# Revit family: Fallrohrstütze DN 80 u. DN100-Set
name_source: partatom
category: HLS-Bauteile
revit_build: Autodesk Revit 2017 (Build: 20190507_1515(x64)
units: mm (PartAtom-declared; Revit-internal decimal feet)

## family parameters
Basisbauteil = Fläche
Beim Laden mit Abzugskörper schneiden = Nein
Bemaßung runder Anschluss = Durchmesser verwenden
Gemeinsam genutzt = Ja
Raumberechnungspunkt = Nein
Teiletyp = Normal

## types (2) — shared parameters
6kt.Flanschmutter = Sechskantmutter : Sechskantmutter M10
6kt.Schraube = 6kt.Schraube DIN EN ISO 4017 : M10x 20 SW17
Abstandswinkel = MEFA Abstandswinkel E : MEFA Abstandswinkel E  L= 25
Abstandswinkeltyp = MEFA Abstandswinkel einfach 42x35x4
Baustoffklasse = B2
Fabrikat = MEFA
Farbe Schalldämmeinlage = Schwarz
Firma = MEFA Befestigungs- und Montagesysteme GmbH
Gewindeplattentyp = M10 35x30
Konsole = Konsole 35-21 : Konsole 35/21/2,  L=263mm
Konsolentyp = C-Profil 35/21
Kurztext1 = Fallrohrstützenbefestigung Set SML
Lochabstand = 55 mm
Länge Konsole = 263 mm  [stored 0.862861 ft]
Material = Stahl
Materialname C-Profil = S250JR
Materialname Platte = S235JR
Mengeneinheit = St
Rohrschellentyp = Maxima PSM
Schalldämmeinlage = Gummi
Stärke Material Schalldämmeinlage = 6 mm
Vorgabe-Ansicht = 1219 mm
WA max. = 260 mm  [stored 0.853018 ft]
max. Temperaturbeständigkeit = 100 °C
max. Wandabstand = 260 mm
max. zul. Last F1 = 0.32 kip
max. zul. Last F2 = 0.16 kip
min. Wandabstand = 75 mm
vpe = 1 St

## per-type parameters (varying)
| type | Abstandsmaß | Artikelnummer | B | EAN | Gewicht | Gewicht pro Bauteil | Kurztext2 | Langloch | Nennweite DN Rohr | Rohrschelle | Setztiefe |
| Fallrohrstütze DN 80 | 140 mm | 4500800 | 135 mm  [stored 0.442913 ft] | 4250928439536 | 1.63 kg | 1.63 kg | DN 80 / 83 mm Wandabstand 75 - 260 mm | 15 x 11 mm | 80 mm  [stored 0.262467 ft] | MEFA RS Maxima PSM, AG M10-M12, Ø65-Ø117 mm, TPE : MEFA RS Maxima PSM, AG M10-M12, Ø84-Ø90 mm, TPE | M10x20 |
| Fallrohrstütze DN100 | 165 mm | 4501000 | 158 mm  [stored 0.518373 ft] | 4250928439543 | 1.70 kg | 1.70 kg | DN 100 / 110 mm Wandabstand 75 - 260 mm | 15x11 mm | 100 mm  [stored 0.328084 ft] | MEFA RS Maxima PSM, AG M10-M12, Ø65-Ø117 mm, TPE : MEFA RS Maxima PSM, AG M10-M12, Ø108-Ø112 mm, TPE |  |

note: [stored X ft] marks values corroborated as IEEE doubles in the binary element streams (Revit-internal decimal feet)

## geometry (parser evidence)
native form markers: Sweep x5
no freeform markers — native parametric forms only
